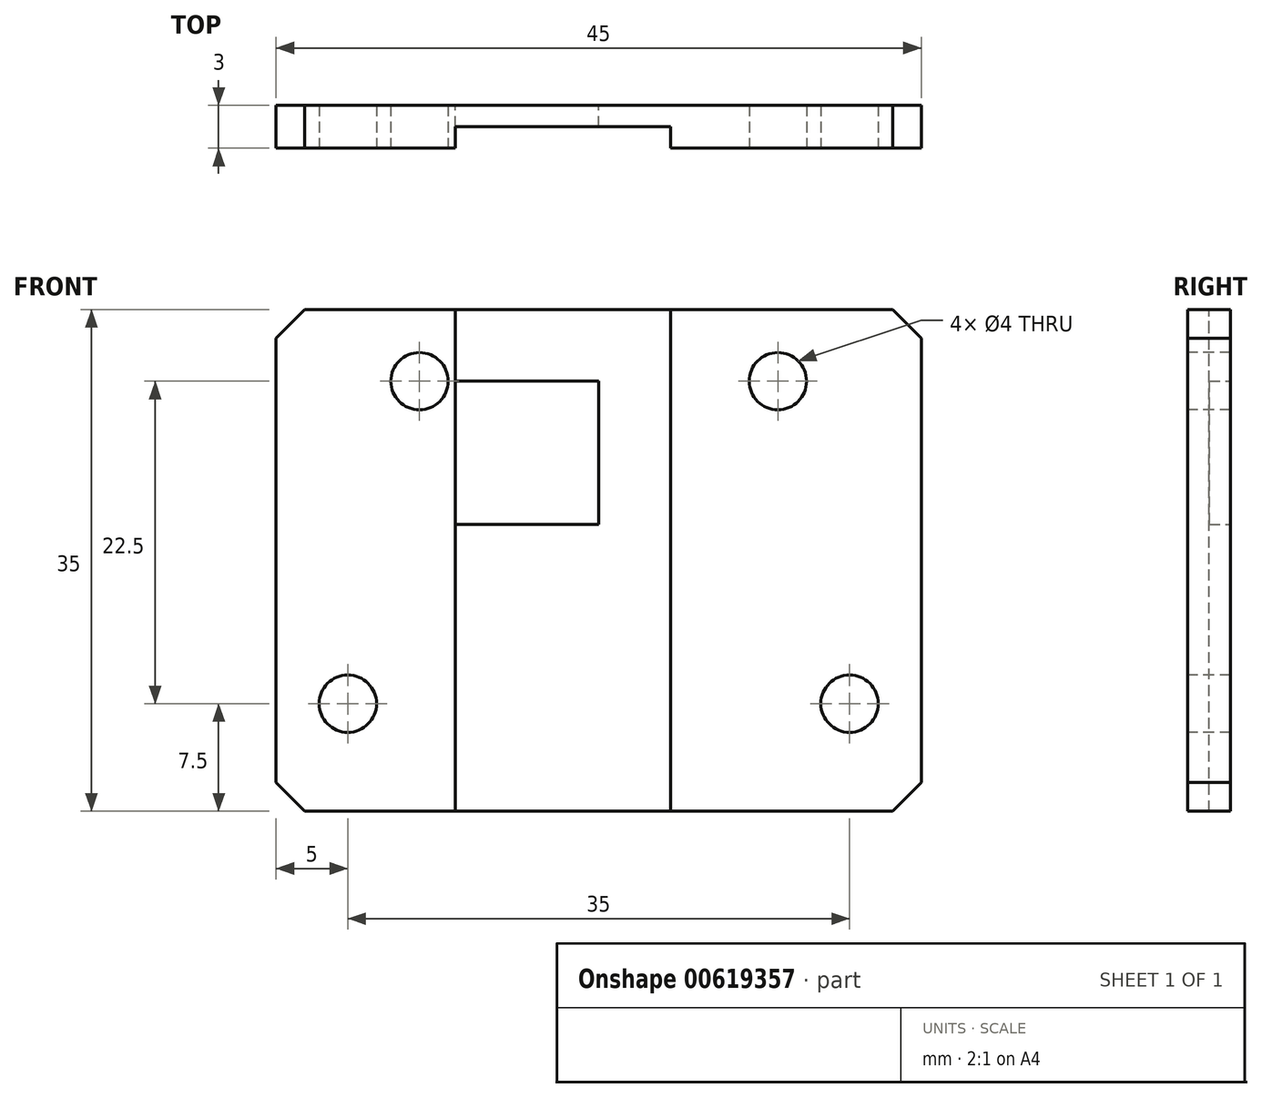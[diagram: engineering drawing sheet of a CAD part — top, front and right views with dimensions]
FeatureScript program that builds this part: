
annotation { "Feature Type Name" : "Feature", "Feature Type Description" : "" }
export const myFeature = defineFeature(function(context is Context, id is Id, definition is map)
    precondition{}
    {
        {
            var Q0;
            Q0=qCreatedBy(makeId("Front.planeOp"),FACE);
            var sketch = newSketch(context, id + "F0", { "sketchPlane" : qUnion([Q0])});
            skLineSegment(sketch, "E0.bottom", {"start": v(-22.5, 20) * mm, "end": v(22.5, 20) * mm});
            skLineSegment(sketch, "E0.top", {"start": v(-22.5, -15) * mm, "end": v(22.5, -15) * mm});
            skLineSegment(sketch, "E0.left", {"start": v(-22.5, 20) * mm, "end": v(-22.5, -15) * mm});
            skLineSegment(sketch, "E0.right", {"start": v(22.5, 20) * mm, "end": v(22.5, -15) * mm});
            skSolve(sketch);
        }
        {
            var Q0;
            Q0=makeQuery(id+"F0.imprint","IMPRINT",FACE,{"disambiguationData":[TD([[makeQuery(id+"F0.imprint","IMPRINT",EDGE,{"derivedFrom":sQuery(id+"F0.wireOp",EDGE,"E0.bottom")}),-1.0]])]});
            extrude(context, id + "F1", {"entities" : qUnion([Q0]), "depth" : 4.5 * mm, "offsetDistance" : 25 * mm});
        }
        {
            var Q0;
            Q0=makeQuery(id+"F1.opExtrude","SWEPT_FACE",FACE,{"disambiguationData":[OSD([sQuery(id+"F0.wireOp",EDGE,"E0.bottom")])]});
            var sketch = newSketch(context, id + "F2", { "sketchPlane" : qUnion([Q0])});
            skLineSegment(sketch, "E1.bottom", {"start": v(-10, -1.5) * mm, "end": v(5, -1.5) * mm});
            skLineSegment(sketch, "E1.top", {"start": v(-10, -3) * mm, "end": v(5, -3) * mm});
            skLineSegment(sketch, "E1.left", {"start": v(-10, -1.5) * mm, "end": v(-10, -3) * mm});
            skLineSegment(sketch, "E1.right", {"start": v(5, -1.5) * mm, "end": v(5, -3) * mm});
            skPoint(sketch, "E1.middle.positionSnap0", {"position": v(22.5, -2.25) * mm});
            skPoint(sketch, "E1.centerSnap0", {"position": v(22.5, -2.25) * mm});
            skSolve(sketch);
        }
        {
            var Q0;
            Q0=qSketchRegion(id+"F2",true);
            extrude(context, id + "F3", {"entities" : qUnion([Q0]), "operationType" : NewBodyOperationType.REMOVE, "endBound" : BoundingType.THROUGH_ALL, "oppositeDirection" : true, "depth" : 25 * mm, "offsetDistance" : 25 * mm});
        }
        {
            var Q0;
            Q0=makeQuery(id+"F1.opExtrude","CAP_FACE",FACE,{"disambiguationData":[OSD([sQuery(id+"F0.wireOp",EDGE,"E0.bottom"),sQuery(id+"F0.wireOp",EDGE,"E0.top"),sQuery(id+"F0.wireOp",EDGE,"E0.left"),sQuery(id+"F0.wireOp",EDGE,"E0.right")])],"isStart":false});
            var sketch = newSketch(context, id + "F4", { "sketchPlane" : qUnion([Q0])});
            skCircle(sketch, "E2", {"center": v(17.5, -7.5) * mm, "radius": 2 * mm});
            skCircle(sketch, "E3.MirrorC", {"center": v(-17.5, -7.5) * mm, "radius": 2 * mm});
            skSolve(sketch);
        }
        {
            var Q0;
            Q0=makeQuery(id+"F1.opExtrude","CAP_FACE",FACE,{"disambiguationData":[OSD([sQuery(id+"F0.wireOp",EDGE,"E0.bottom"),sQuery(id+"F0.wireOp",EDGE,"E0.top"),sQuery(id+"F0.wireOp",EDGE,"E0.left"),sQuery(id+"F0.wireOp",EDGE,"E0.right")])],"isStart":true});
            var sketch = newSketch(context, id + "F5", { "sketchPlane" : qUnion([Q0])});
            skLineSegment(sketch, "E4.bottom", {"start": v(10, 5) * mm, "end": v(0, 5) * mm});
            skLineSegment(sketch, "E4.top", {"start": v(10, 15) * mm, "end": v(0, 15) * mm});
            skLineSegment(sketch, "E4.left", {"start": v(10, 5) * mm, "end": v(10, 15) * mm});
            skLineSegment(sketch, "E4.right", {"start": v(0, 5) * mm, "end": v(0, 15) * mm});
            skPoint(sketch, "E4.middle", {"position": v(0, 7) * mm});
            skSolve(sketch);
        }
        {
            var Q0;
            Q0=qSketchRegion(id+"F5",true);
            extrude(context, id + "F6", {"entities" : qUnion([Q0]), "operationType" : NewBodyOperationType.REMOVE, "oppositeDirection" : true, "depth" : 3 * mm, "offsetDistance" : 25 * mm});
        }
        {
            var Q0;
            Q0=makeQuery(id+"F1.opExtrude","SWEPT_EDGE",EDGE,{"disambiguationData":[OSD([sQuery(id+"F0.wireOp",EDGE,"E0.bottom"),sQuery(id+"F0.wireOp",EDGE,"E0.left")])]});
            var Q1;
            Q1=makeQuery(id+"F1.opExtrude","SWEPT_EDGE",EDGE,{"disambiguationData":[OSD([sQuery(id+"F0.wireOp",EDGE,"E0.bottom"),sQuery(id+"F0.wireOp",EDGE,"E0.right")])]});
            var Q2;
            Q2=makeQuery(id+"F1.opExtrude","SWEPT_EDGE",EDGE,{"disambiguationData":[OSD([sQuery(id+"F0.wireOp",EDGE,"E0.top"),sQuery(id+"F0.wireOp",EDGE,"E0.right")])]});
            var Q3;
            Q3=makeQuery(id+"F1.opExtrude","SWEPT_EDGE",EDGE,{"disambiguationData":[OSD([sQuery(id+"F0.wireOp",EDGE,"E0.top"),sQuery(id+"F0.wireOp",EDGE,"E0.left")])]});
            chamfer(context, id + "F7", {"entities" : qUnion([Q0, Q1, Q2, Q3]), "width" : 2 * mm, "tangentPropagation" : true});
        }
        {
            var Q0;
            Q0=makeQuery(id+"F1.opExtrude","SWEPT_FACE",FACE,{"disambiguationData":[OSD([sQuery(id+"F0.wireOp",EDGE,"E0.top")])]});
            var sketch = newSketch(context, id + "F8", { "sketchPlane" : qUnion([Q0])});
            skLineSegment(sketch, "E5.bottom", {"start": v(-22.5, 4.5) * mm, "end": v(22.72, 4.5) * mm});
            skLineSegment(sketch, "E5.top", {"start": v(-22.5, 3) * mm, "end": v(22.72, 3) * mm});
            skLineSegment(sketch, "E5.left", {"start": v(-22.5, 4.5) * mm, "end": v(-22.5, 3) * mm});
            skLineSegment(sketch, "E5.right", {"start": v(22.72, 4.5) * mm, "end": v(22.72, 3) * mm});
            skSolve(sketch);
        }
        {
            var Q0;
            Q0 = qSketchRegion(id + "F8", true);
            extrude(context, id + "F9", {"entities" : qUnion([Q0]), "operationType" : NewBodyOperationType.REMOVE, "endBound" : BoundingType.THROUGH_ALL, "oppositeDirection" : true, "depth" : 25 * mm, "offsetDistance" : 25 * mm});
        }
        {
            var Q0;
            Q0 = qSketchRegion(id + "F4", true);
            extrude(context, id + "F10", {"entities" : qUnion([Q0]), "operationType" : NewBodyOperationType.REMOVE, "oppositeDirection" : true, "depth" : 25 * mm, "offsetDistance" : 25 * mm});
        }
        {
            var Q0;
            {var subQ1=sQuery(id+"F0.wireOp",EDGE,"E0.right");Q0=makeQuery(id+"F9.boolean.opBoolean","COPY",FACE,{"disambiguationData":[TD([makeQuery(id+"F1.opExtrude","SWEPT_FACE",FACE,{"disambiguationData":[OSD([subQ1])]})])],"derivedFrom":makeQuery(id+"F9.opExtrude","SWEPT_FACE",FACE,{"disambiguationData":[OSD([sQuery(id+"F8.wireOp",EDGE,"E5.top")])]})});}
            var sketch = newSketch(context, id + "F11", { "sketchPlane" : qUnion([Q0])});
            skCircle(sketch, "E6", {"center": v(12.5, 15) * mm, "radius": 2 * mm});
            skCircle(sketch, "E7", {"center": v(-12.5, 15) * mm, "radius": 2 * mm});
            skSolve(sketch);
        }
        {
            var Q0;
            Q0 = qSketchRegion(id + "F11", true);
            extrude(context, id + "F12", {"entities" : qUnion([Q0]), "operationType" : NewBodyOperationType.REMOVE, "endBound" : BoundingType.THROUGH_ALL, "oppositeDirection" : true, "depth" : 25 * mm, "offsetDistance" : 25 * mm});
        }
    });
